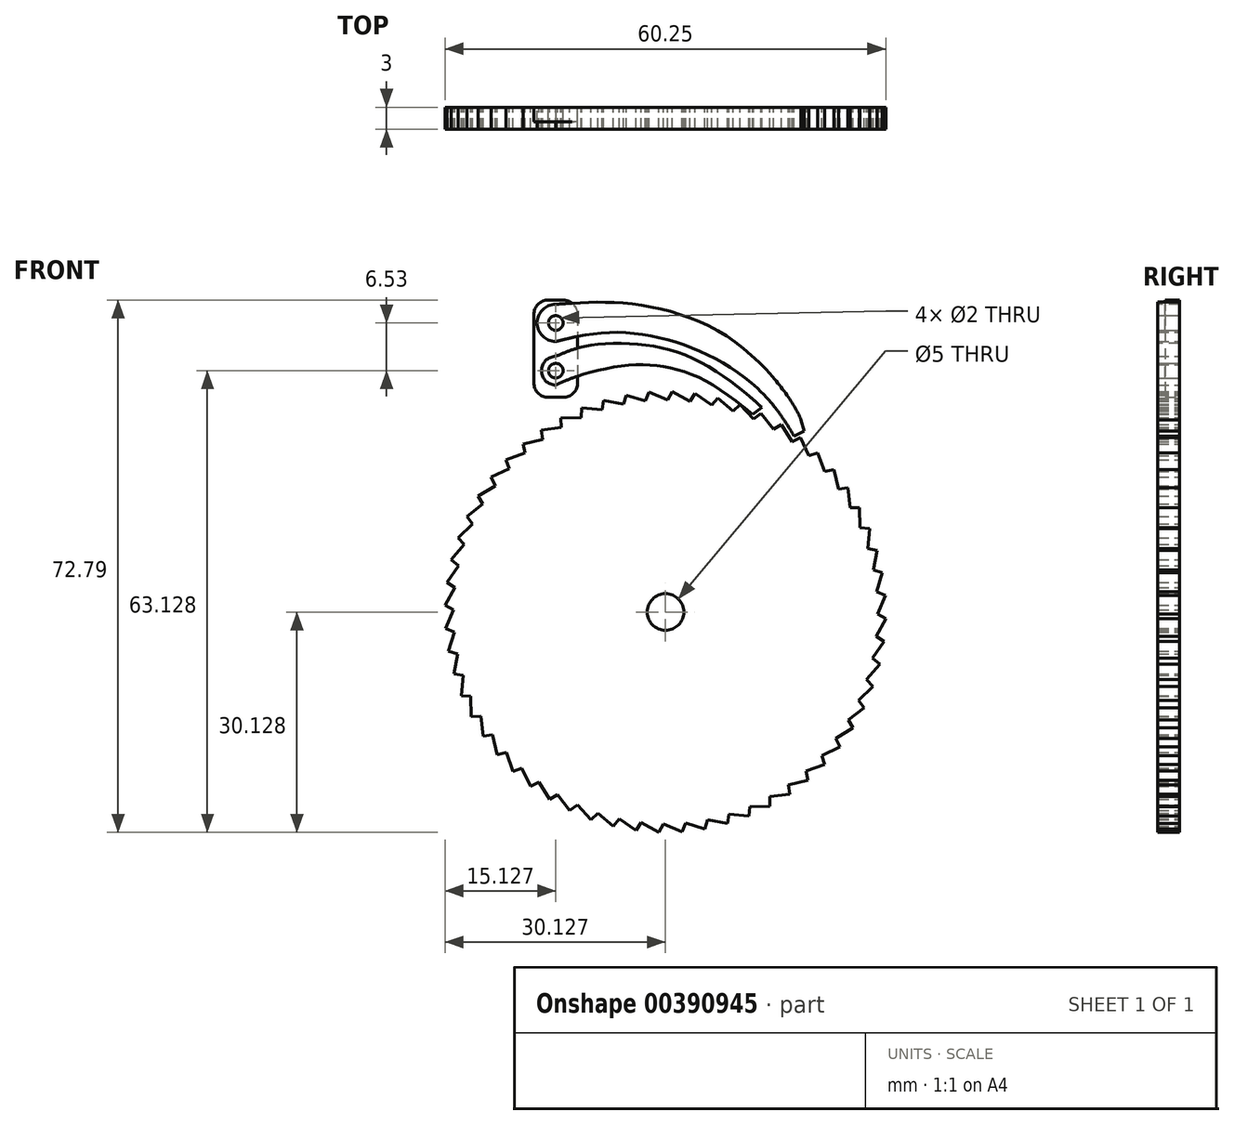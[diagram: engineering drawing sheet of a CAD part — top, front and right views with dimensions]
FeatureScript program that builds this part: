
annotation { "Feature Type Name" : "Feature", "Feature Type Description" : "" }
export const myFeature = defineFeature(function(context is Context, id is Id, definition is map)
    precondition{}
    {
        {
            var Q0;
            Q0=qCreatedBy(makeId("Front.planeOp"),FACE);
            var sketch = newSketch(context, id + "F0", { "sketchPlane" : qUnion([Q0])});
            skCircle(sketch, "E0", {"center": v(-79.93, -38.75) * mm, "radius": 60 * mm, "construction": true});
            skCircle(sketch, "E1", {"center": v(10.07, -17.75) * mm, "radius": 25 * mm, "construction": true});
            skCircle(sketch, "E2", {"center": v(10.07, -17.75) * mm, "radius": 29 * mm});
            skPoint(sketch, "E3.8.internal.snap0", {"position": v(-2.56, 19.52) * mm});
            skPoint(sketch, "E3.13.internal.snap0", {"position": v(-2.56, 19.52) * mm});
            skLineSegment(sketch, "E4", {"start": v(10.07, -17.75) * mm, "end": v(22.12, 8.62) * mm, "construction": true});
            skLineSegment(sketch, "E5", {"start": v(10.07, -17.75) * mm, "end": v(24.82, 7.22) * mm, "construction": true});
            skLineSegment(sketch, "E6", {"start": v(23.15, 9.4) * mm, "end": v(22.12, 8.62) * mm});
            skLineSegment(sketch, "E7", {"start": v(24.82, 7.22) * mm, "end": v(23.15, 9.4) * mm});
            skLineSegment(sketch, "E8.bottom", {"start": v(-159.93, 46.25) * mm, "end": v(87.02, 46.25) * mm, "construction": true});
            skLineSegment(sketch, "E8.top", {"start": v(-156.89, -123.75) * mm, "end": v(90.07, -123.75) * mm, "construction": true});
            skLineSegment(sketch, "E8.left", {"start": v(-164.93, 48.24) * mm, "end": v(-164.93, -123.75) * mm, "construction": true});
            skLineSegment(sketch, "E8.right", {"start": v(85.07, 48.24) * mm, "end": v(85.07, -123.75) * mm, "construction": true});
            skLineSegment(sketch, "E9.bottom", {"start": v(-5.93, 24.91) * mm, "end": v(-3.93, 24.91) * mm});
            skLineSegment(sketch, "E9.top", {"start": v(-5.93, 11.6) * mm, "end": v(-3.93, 11.6) * mm});
            skLineSegment(sketch, "E9.left", {"start": v(-7.93, 22.91) * mm, "end": v(-7.93, 13.6) * mm});
            skLineSegment(sketch, "E9.right", {"start": v(-1.93, 22.91) * mm, "end": v(-1.93, 13.6) * mm});
            skPoint(sketch, "E10.visualSharp", {"position": v(-7.93, 24.91) * mm});
            skArc(sketch, "E10.filletArc", {"start": v(-5.93, 24.91) * mm, "mid": v(-7.35, 24.32) * mm, "end": v(-7.93, 22.91) * mm});
            skPoint(sketch, "E11.visualSharp", {"position": v(-1.93, 24.91) * mm});
            skArc(sketch, "E11.filletArc", {"start": v(-1.93, 22.91) * mm, "mid": v(-2.52, 24.32) * mm, "end": v(-3.93, 24.91) * mm});
            skPoint(sketch, "E12.visualSharp", {"position": v(-7.93, 11.6) * mm});
            skArc(sketch, "E12.filletArc", {"start": v(-7.93, 13.6) * mm, "mid": v(-7.35, 12.18) * mm, "end": v(-5.93, 11.6) * mm});
            skPoint(sketch, "E13.visualSharp", {"position": v(-1.93, 11.6) * mm});
            skArc(sketch, "E13.filletArc", {"start": v(-3.93, 11.6) * mm, "mid": v(-2.52, 12.18) * mm, "end": v(-1.93, 13.6) * mm});
            skFitSpline(sketch, "E14", {"points": [v(-4.97, 24.32) * mm, v(5.32, 24.39) * mm, v(18.74, 19.77) * mm, v(27.65, 10.38) * mm, v(29.62, 5.86) * mm], "startDerivative": vector(39.27, 3.14) * mm, "endDerivative": vector(7.91, -23.77) * mm});
            skFitSpline(sketch, "E15", {"points": [v(-4.96, 19.24) * mm, v(2.23, 20.47) * mm, v(10.22, 19.52) * mm, v(18.16, 16.18) * mm, v(24.52, 10.86) * mm, v(28.4, 5) * mm], "startDerivative": vector(36.53, 9.13) * mm, "endDerivative": vector(18.3, -31.67) * mm});
            skArc(sketch, "E16", {"start": v(-4.97, 24.32) * mm, "mid": v(-7.47, 21.78) * mm, "end": v(-4.96, 19.24) * mm});
            skArc(sketch, "E17", {"start": v(-4.96, 17.2) * mm, "mid": v(-6.89, 15.25) * mm, "end": v(-4.96, 13.3) * mm});
            skFitSpline(sketch, "E18", {"points": [v(-4.96, 17.2) * mm, v(-0.68, 18.63) * mm, v(6.57, 18.85) * mm, v(14.38, 16.66) * mm, v(21.51, 11.76) * mm, v(24.36, 9.15) * mm], "startDerivative": vector(23.14, 10.28) * mm, "endDerivative": vector(15.74, -15.3) * mm});
            skFitSpline(sketch, "E19", {"points": [v(-4.96, 13.3) * mm, v(-1.21, 14.73) * mm, v(4.78, 15.99) * mm, v(9.97, 15.78) * mm, v(15.6, 13.84) * mm, v(23.2, 8.25) * mm], "startDerivative": vector(20.88, 10.16) * mm, "endDerivative": vector(30.85, -25.54) * mm});
            skLineSegment(sketch, "E20", {"start": v(23.26, 10.21) * mm, "end": v(21.97, 9.26) * mm});
            skLineSegment(sketch, "E21", {"start": v(27.65, 6.29) * mm, "end": v(29.03, 7) * mm});
            skLineSegment(sketch, "E22", {"start": v(29.03, 7) * mm, "end": v(28.62, 8.54) * mm});
            skCircle(sketch, "E23", {"center": v(-4.93, 21.78) * mm, "radius": 1 * mm});
            skCircle(sketch, "E24", {"center": v(-4.93, 15.25) * mm, "radius": 1 * mm});
            skCircle(sketch, "E25", {"center": v(0.3, -66.8) * mm, "radius": 25 * mm, "construction": true});
            skCircle(sketch, "E26", {"center": v(10.07, -17.75) * mm, "radius": 2.5 * mm});
            skLineSegment(sketch, "E27", {"start": v(20.62, 10.38) * mm, "end": v(22.08, 8.82) * mm});
            skLineSegment(sketch, "E28", {"start": v(22.08, 8.82) * mm, "end": v(23, 9.52) * mm});
            skLineSegment(sketch, "E29", {"start": v(23, 9.52) * mm, "end": v(21.51, 11.76) * mm});
            skLineSegment(sketch, "E30", {"start": v(22.65, 12.81) * mm, "end": v(24.85, 7.47) * mm});
            skLineSegment(sketch, "E31", {"start": v(24.85, 7.47) * mm, "end": v(25.8, 8) * mm});
            skLineSegment(sketch, "E32", {"start": v(25.8, 8) * mm, "end": v(24.7, 14.42) * mm});
            skSolve(sketch);
        }
        {
            var Q0;
            {var subQ5=sQuery(id+"F0.wireOp",EDGE,"E7");Q0=makeQuery(id+"F0.imprint","IMPRINT",FACE,{"disambiguationData":[TD([[makeQuery(id+"F0.imprint","IMPRINT",EDGE,{"derivedFrom":subQ5}),1.0]])]});}
            extrude(context, id + "F1", {"entities" : qUnion([Q0]), "depth" : 3 * mm});
        }
        {
            var Q0;
            Q0=makeQuery(id+"F1.opExtrude","SWEPT_BODY",BODY,{"disambiguationData":[OSD([sQuery(id+"F0.wireOp",EDGE,"E2"),sQuery(id+"F0.wireOp",EDGE,"E6"),sQuery(id+"F0.wireOp",EDGE,"E7")])]});
            var Q1;
            Q1=sQuery(id+"F0.wireOp",EDGE,"E2");
            circularPattern(context, id + "F2", {"entities" : qUnion([Q0]), "axis" : qUnion([Q1]), "angle" : 360 * degree, "instanceCount" : 60, "equalSpace" : true});
        }
        {
            var Q0;
            {var subQ0=sQuery(id+"F0.wireOp",EDGE,"E2");var subQ1=makeQuery(id+"F0.imprint","INTERSECT",VERTEX,{"derivedFrom":[subQ0,sQuery(id+"F0.wireOp",EDGE,"E6")]});Q0=makeQuery(id+"F0.imprint","IMPRINT",FACE,{"disambiguationData":[TD([[makeQuery(id+"F0.imprint","IMPRINT",EDGE,{"disambiguationData":[TD([[subQ1,1.0]])],"derivedFrom":subQ0}),1.0]])]});}
            extrude(context, id + "F3", {"entities" : qUnion([Q0]), "operationType" : NewBodyOperationType.ADD, "depth" : 3 * mm});
        }
        {
            var Q0;
            {var subQ1=sQuery(id+"F0.wireOp",EDGE,"E9.bottom");Q0=makeQuery(id+"F0.imprint","IMPRINT",FACE,{"disambiguationData":[TD([[makeQuery(id+"F0.imprint","IMPRINT",EDGE,{"derivedFrom":subQ1}),-1.0]])]});}
            var Q1;
            {var subQ0=sQuery(id+"F0.wireOp",EDGE,"E16");Q1=makeQuery(id+"F0.imprint","IMPRINT",FACE,{"disambiguationData":[TD([[makeQuery(id+"F0.imprint","IMPRINT",EDGE,{"derivedFrom":subQ0}),1.0]])]});}
            var Q2;
            {var subQ5=sQuery(id+"F0.wireOp",EDGE,"E17");Q2=makeQuery(id+"F0.imprint","IMPRINT",FACE,{"disambiguationData":[TD([[makeQuery(id+"F0.imprint","IMPRINT",EDGE,{"derivedFrom":subQ5}),1.0]])]});}
            extrude(context, id + "F4", {"entities" : qUnion([Q0, Q1, Q2]), "depth" : 2 * mm});
        }
        {
            var Q0;
            {var subQ0=sQuery(id+"F0.wireOp",EDGE,"E16");Q0=makeQuery(id+"F0.imprint","IMPRINT",FACE,{"disambiguationData":[TD([[makeQuery(id+"F0.imprint","IMPRINT",EDGE,{"derivedFrom":subQ0}),1.0]])]});}
            var Q1;
            {var subQ0=sQuery(id+"F0.wireOp",EDGE,"E21");Q1=makeQuery(id+"F0.imprint","IMPRINT",FACE,{"disambiguationData":[TD([[makeQuery(id+"F0.imprint","IMPRINT",EDGE,{"derivedFrom":subQ0}),1.0]])]});}
            var Q2;
            {var subQ2=sQuery(id+"F0.wireOp",EDGE,"E9.right");var subQ7=sQuery(id+"F0.wireOp",EDGE,"E11.filletArc");var subQ9=makeQuery(id+"F0.imprint","INTERSECT",VERTEX,{"derivedFrom":[subQ2,subQ7]});Q2=makeQuery(id+"F0.imprint","IMPRINT",FACE,{"disambiguationData":[TD([[makeQuery(id+"F0.imprint","IMPRINT",EDGE,{"disambiguationData":[TD([[subQ9,-1.0]])],"derivedFrom":subQ2}),1.0]])]});}
            extrude(context, id + "F5", {"entities" : qUnion([Q0, Q1, Q2]), "depth" : 3 * mm});
        }
        {
            var Q0;
            {var subQ5=sQuery(id+"F0.wireOp",EDGE,"E17");Q0=makeQuery(id+"F0.imprint","IMPRINT",FACE,{"disambiguationData":[TD([[makeQuery(id+"F0.imprint","IMPRINT",EDGE,{"derivedFrom":subQ5}),1.0]])]});}
            var Q1;
            {var subQ5=sQuery(id+"F0.wireOp",EDGE,"E20");Q1=makeQuery(id+"F0.imprint","IMPRINT",FACE,{"disambiguationData":[TD([[makeQuery(id+"F0.imprint","IMPRINT",EDGE,{"derivedFrom":subQ5}),-1.0]])]});}
            var Q2;
            {var subQ0=sQuery(id+"F0.wireOp",EDGE,"E19");var subQ2=sQuery(id+"F0.wireOp",EDGE,"E9.right");var subQ3=makeQuery(id+"F0.imprint","INTERSECT",VERTEX,{"derivedFrom":[subQ2,subQ0]});Q2=makeQuery(id+"F0.imprint","IMPRINT",FACE,{"disambiguationData":[TD([[makeQuery(id+"F0.imprint","IMPRINT",EDGE,{"disambiguationData":[TD([[subQ3,1.0]])],"derivedFrom":subQ2}),1.0]])]});}
            extrude(context, id + "F6", {"entities" : qUnion([Q0, Q1, Q2]), "depth" : 3 * mm});
        }
    });
